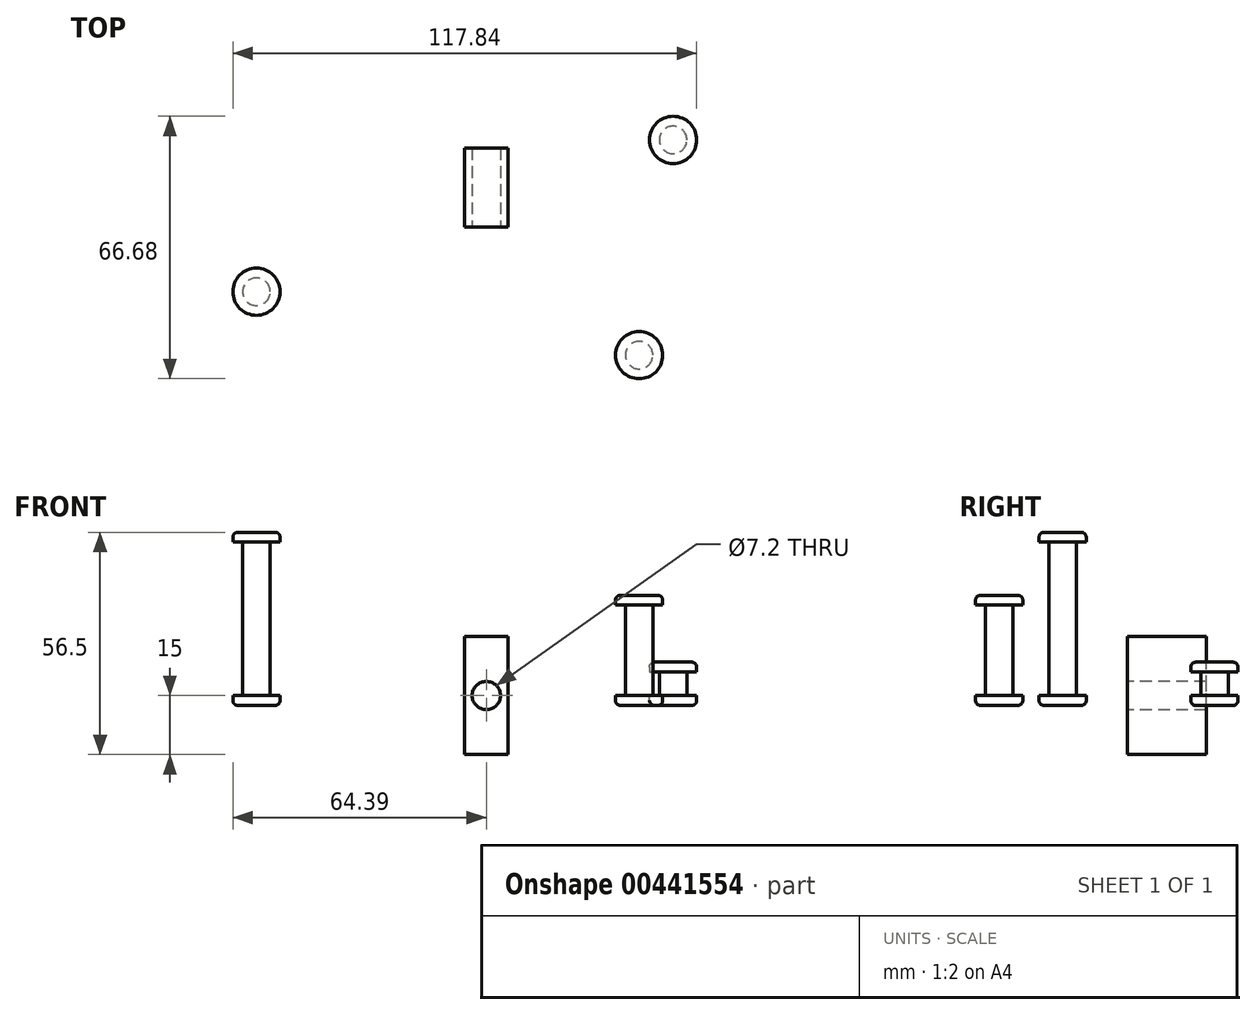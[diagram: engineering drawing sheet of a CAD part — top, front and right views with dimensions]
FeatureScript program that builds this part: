
annotation { "Feature Type Name" : "Feature", "Feature Type Description" : "" }
export const myFeature = defineFeature(function(context is Context, id is Id, definition is map)
    precondition{}
    {
        {
            var Q0;
            Q0=qCreatedBy(makeId("Front.planeOp"),FACE);
            var sketch = newSketch(context, id + "F0", { "sketchPlane" : qUnion([Q0])});
            skLineSegment(sketch, "E0.bottom", {"start": v(5.5, -15) * mm, "end": v(-5.5, -15) * mm});
            skLineSegment(sketch, "E0.top", {"start": v(5.5, 15) * mm, "end": v(-5.5, 15) * mm});
            skLineSegment(sketch, "E0.left", {"start": v(5.5, -15) * mm, "end": v(5.5, 15) * mm});
            skLineSegment(sketch, "E0.right", {"start": v(-5.5, -15) * mm, "end": v(-5.5, 15) * mm});
            skPoint(sketch, "E0.middle", {"position": v(0, 0) * mm});
            skSolve(sketch);
        }
        {
            var Q0;
            Q0 = qSketchRegion(id + "F0", true);
            extrude(context, id + "F1", {"entities" : qUnion([Q0]), "oppositeDirection" : true, "depth" : 20 * mm});
        }
        {
            var Q0;
            Q0=makeQuery(id+"F1.opExtrude","CAP_FACE",FACE,{"disambiguationData":[OSD([sQuery(id+"F0.wireOp",EDGE,"E0.bottom"),sQuery(id+"F0.wireOp",EDGE,"E0.top"),sQuery(id+"F0.wireOp",EDGE,"E0.left"),sQuery(id+"F0.wireOp",EDGE,"E0.right")])],"isStart":true});
            var sketch = newSketch(context, id + "F2", { "sketchPlane" : qUnion([Q0])});
            skCircle(sketch, "E1", {"center": v(0, 0) * mm, "radius": 3.6 * mm});
            skSolve(sketch);
        }
        {
            var Q0;
            Q0 = qSketchRegion(id + "F2", true);
            extrude(context, id + "F3", {"entities" : qUnion([Q0]), "operationType" : NewBodyOperationType.REMOVE, "oppositeDirection" : true, "depth" : 25.4 * mm});
        }
        {
            var Q0;
            Q0=qCreatedBy(makeId("Top.planeOp"),FACE);
            var sketch = newSketch(context, id + "F4", { "sketchPlane" : qUnion([Q0])});
            skCircle(sketch, "E2", {"center": v(-58.4, -16.48) * mm, "radius": 3.5 * mm});
            skSolve(sketch);
        }
        {
            var Q0;
            Q0 = qSketchRegion(id + "F4", true);
            extrude(context, id + "F5", {"entities" : qUnion([Q0]), "depth" : 39 * mm});
        }
        {
            var Q0;
            Q0=makeQuery(id+"F5.opExtrude","CAP_FACE",FACE,{"disambiguationData":[OSD([sQuery(id+"F4.wireOp",EDGE,"E2")])],"isStart":false});
            var sketch = newSketch(context, id + "F6", { "sketchPlane" : qUnion([Q0])});
            skCircle(sketch, "E3", {"center": v(-58.4, -16.48) * mm, "radius": 6 * mm});
            skSolve(sketch);
        }
        {
            var Q0;
            Q0 = qSketchRegion(id + "F6", true);
            extrude(context, id + "F7", {"entities" : qUnion([Q0]), "operationType" : NewBodyOperationType.ADD, "depth" : 2.5 * mm});
        }
        {
            var Q0;
            Q0=makeQuery(id+"F5.opExtrude","CAP_FACE",FACE,{"disambiguationData":[OSD([sQuery(id+"F4.wireOp",EDGE,"E2")])],"isStart":true});
            var sketch = newSketch(context, id + "F8", { "sketchPlane" : qUnion([Q0])});
            skCircle(sketch, "E4", {"center": v(-58.4, 16.48) * mm, "radius": 6 * mm});
            skSolve(sketch);
        }
        {
            var Q0;
            Q0 = qSketchRegion(id + "F8", true);
            extrude(context, id + "F9", {"entities" : qUnion([Q0]), "operationType" : NewBodyOperationType.ADD, "depth" : 2.5 * mm});
        }
        {
            var Q0;
            Q0=makeQuery(id+"F9.opExtrude","CAP_EDGE",EDGE,{"disambiguationData":[OSD([sQuery(id+"F8.wireOp",EDGE,"E4")])],"isStart":false});
            var Q1;
            Q1=makeQuery(id+"F7.opExtrude","CAP_EDGE",EDGE,{"disambiguationData":[OSD([sQuery(id+"F6.wireOp",EDGE,"E3")])],"isStart":false});
            fillet(context, id + "F10", {"entities" : qUnion([Q0, Q1]), "radius" : 1.27 * mm, "tangentPropagation" : true, "allowEdgeOverflow" : false});
        }
        {
            var Q0;
            Q0=qCreatedBy(makeId("Top.planeOp"),FACE);
            var sketch = newSketch(context, id + "F11", { "sketchPlane" : qUnion([Q0])});
            skCircle(sketch, "E5", {"center": v(38.8, -32.6) * mm, "radius": 3.5 * mm});
            skSolve(sketch);
        }
        {
            var Q0;
            Q0 = qSketchRegion(id + "F11", true);
            extrude(context, id + "F12", {"entities" : qUnion([Q0]), "depth" : 23 * mm});
        }
        {
            var Q0;
            Q0=makeQuery(id+"F12.opExtrude","CAP_FACE",FACE,{"disambiguationData":[OSD([sQuery(id+"F11.wireOp",EDGE,"E5")])],"isStart":false});
            var sketch = newSketch(context, id + "F13", { "sketchPlane" : qUnion([Q0])});
            skCircle(sketch, "E6", {"center": v(38.8, -32.6) * mm, "radius": 6 * mm});
            skSolve(sketch);
        }
        {
            var Q0;
            Q0 = qSketchRegion(id + "F13", true);
            extrude(context, id + "F14", {"entities" : qUnion([Q0]), "operationType" : NewBodyOperationType.ADD, "depth" : 2.5 * mm});
        }
        {
            var Q0;
            Q0=makeQuery(id+"F12.opExtrude","CAP_FACE",FACE,{"disambiguationData":[OSD([sQuery(id+"F11.wireOp",EDGE,"E5")])],"isStart":true});
            var sketch = newSketch(context, id + "F15", { "sketchPlane" : qUnion([Q0])});
            skCircle(sketch, "E7", {"center": v(38.8, 32.6) * mm, "radius": 6 * mm});
            skSolve(sketch);
        }
        {
            var Q0;
            Q0 = qSketchRegion(id + "F15", true);
            extrude(context, id + "F16", {"entities" : qUnion([Q0]), "operationType" : NewBodyOperationType.ADD, "depth" : 2.5 * mm});
        }
        {
            var Q0;
            Q0=makeQuery(id+"F16.opExtrude","CAP_EDGE",EDGE,{"disambiguationData":[OSD([sQuery(id+"F15.wireOp",EDGE,"E7")])],"isStart":false});
            var Q1;
            Q1=makeQuery(id+"F14.opExtrude","CAP_EDGE",EDGE,{"disambiguationData":[OSD([sQuery(id+"F13.wireOp",EDGE,"E6")])],"isStart":false});
            fillet(context, id + "F17", {"entities" : qUnion([Q0, Q1]), "radius" : 1.27 * mm, "tangentPropagation" : true, "allowEdgeOverflow" : false});
        }
        {
            var Q0;
            Q0=qCreatedBy(makeId("Top.planeOp"),FACE);
            var sketch = newSketch(context, id + "F18", { "sketchPlane" : qUnion([Q0])});
            skCircle(sketch, "E8", {"center": v(47.45, 22.08) * mm, "radius": 3.5 * mm});
            skSolve(sketch);
        }
        {
            var Q0;
            Q0 = qSketchRegion(id + "F18", true);
            extrude(context, id + "F19", {"entities" : qUnion([Q0]), "depth" : 6 * mm});
        }
        {
            var Q0;
            Q0=makeQuery(id+"F19.opExtrude","CAP_FACE",FACE,{"disambiguationData":[OSD([sQuery(id+"F18.wireOp",EDGE,"E8")])],"isStart":true});
            var sketch = newSketch(context, id + "F20", { "sketchPlane" : qUnion([Q0])});
            skCircle(sketch, "E9", {"center": v(47.45, -22.08) * mm, "radius": 6 * mm});
            skSolve(sketch);
        }
        {
            var Q0;
            Q0 = qSketchRegion(id + "F20", true);
            extrude(context, id + "F21", {"entities" : qUnion([Q0]), "operationType" : NewBodyOperationType.ADD, "depth" : 2.5 * mm});
        }
        {
            var Q0;
            Q0=makeQuery(id+"F19.opExtrude","CAP_FACE",FACE,{"disambiguationData":[OSD([sQuery(id+"F18.wireOp",EDGE,"E8")])],"isStart":false});
            var sketch = newSketch(context, id + "F22", { "sketchPlane" : qUnion([Q0])});
            skCircle(sketch, "E10", {"center": v(47.45, 22.08) * mm, "radius": 6 * mm});
            skSolve(sketch);
        }
        {
            var Q0;
            Q0 = qSketchRegion(id + "F22", true);
            extrude(context, id + "F23", {"entities" : qUnion([Q0]), "operationType" : NewBodyOperationType.ADD, "depth" : 2.5 * mm});
        }
        {
            var Q0;
            Q0=makeQuery(id+"F23.opExtrude","CAP_EDGE",EDGE,{"disambiguationData":[OSD([sQuery(id+"F22.wireOp",EDGE,"E10")])],"isStart":false});
            var Q1;
            Q1=makeQuery(id+"F21.opExtrude","CAP_EDGE",EDGE,{"disambiguationData":[OSD([sQuery(id+"F20.wireOp",EDGE,"E9")])],"isStart":false});
            fillet(context, id + "F24", {"entities" : qUnion([Q0, Q1]), "radius" : 1.27 * mm, "tangentPropagation" : true, "allowEdgeOverflow" : false});
        }
    });
